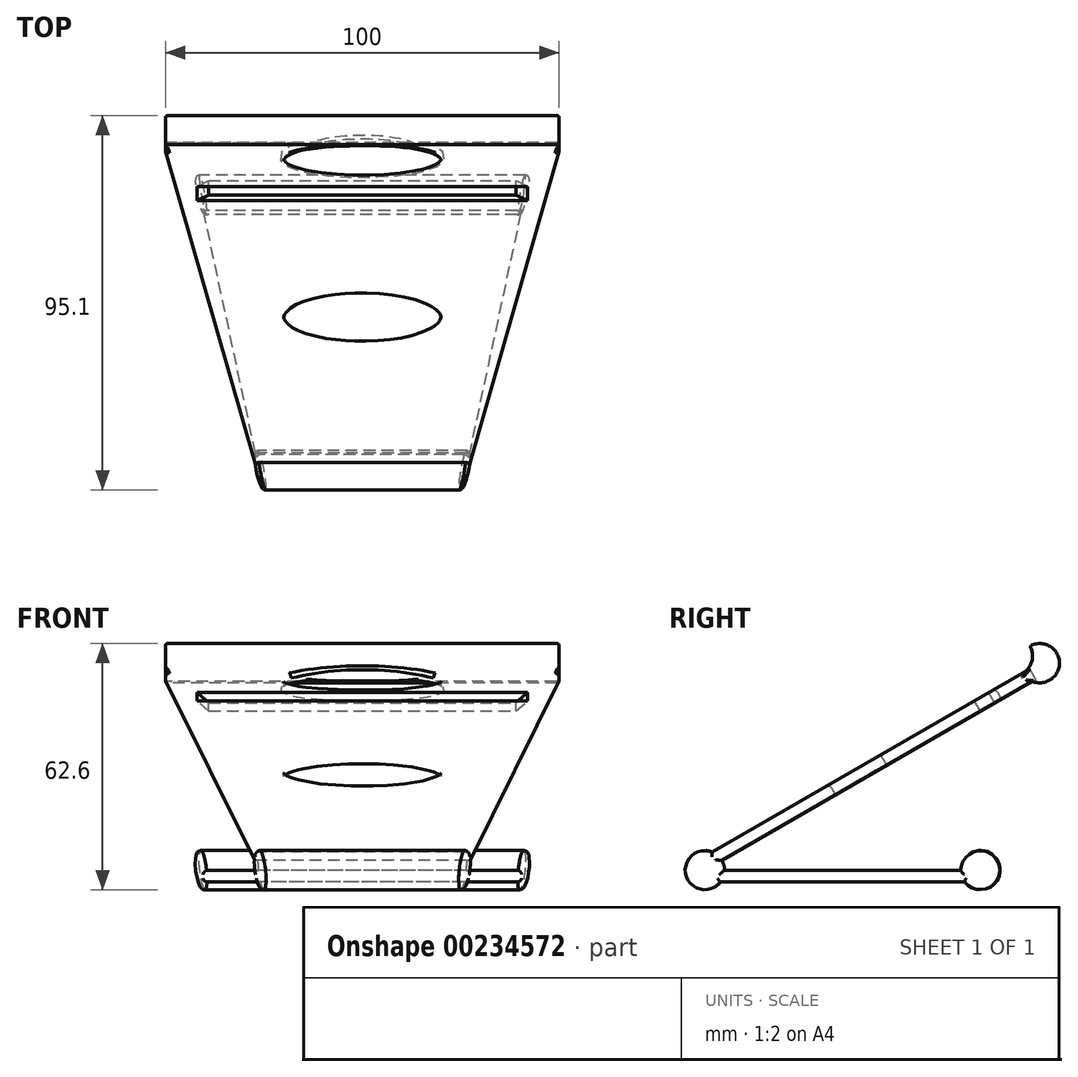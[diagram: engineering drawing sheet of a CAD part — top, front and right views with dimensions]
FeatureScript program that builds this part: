
annotation { "Feature Type Name" : "Feature", "Feature Type Description" : "" }
export const myFeature = defineFeature(function(context is Context, id is Id, definition is map)
    precondition{}
    {
        {
            var Q0;
            Q0=qCreatedBy(makeId("Right.planeOp"),FACE);
            var sketch = newSketch(context, id + "F0", { "sketchPlane" : qUnion([Q0])});
            skLineSegment(sketch, "E0.bottom", {"start": v(-35, -1.5) * mm, "end": v(35, -1.5) * mm});
            skLineSegment(sketch, "E0.top", {"start": v(-35, 1.5) * mm, "end": v(35, 1.5) * mm});
            skLineSegment(sketch, "E0.left", {"start": v(-35, -1.5) * mm, "end": v(-35, 1.5) * mm});
            skLineSegment(sketch, "E0.right", {"start": v(35, -1.5) * mm, "end": v(35, 1.5) * mm});
            skPoint(sketch, "E0.middle", {"position": v(0, 0) * mm});
            skLineSegment(sketch, "E1", {"start": v(-35, 1.5) * mm, "end": v(51.6, 51.5) * mm});
            skLineSegment(sketch, "E2", {"start": v(51.6, 51.5) * mm, "end": v(50.1, 54.1) * mm});
            skLineSegment(sketch, "E3", {"start": v(50.1, 54.1) * mm, "end": v(-36.5, 4.1) * mm});
            skLineSegment(sketch, "E4", {"start": v(-36.5, 4.1) * mm, "end": v(-35, 1.5) * mm});
            skCircle(sketch, "E5", {"center": v(-35, 1.5) * mm, "radius": 5 * mm});
            skCircle(sketch, "E6", {"center": v(35, 1.5) * mm, "radius": 5 * mm});
            skCircle(sketch, "E7", {"center": v(50.1, 54.1) * mm, "radius": 5 * mm});
            skLineSegment(sketch, "E8", {"start": v(47.6, 58.43) * mm, "end": v(47.6, 58.43) * mm});
            skLineSegment(sketch, "E9", {"start": v(45.77, 51.6) * mm, "end": v(45.77, 51.6) * mm});
            skArc(sketch, "E10.filletArc", {"start": v(45.77, 51.6) * mm, "mid": v(48.1, 54.63) * mm, "end": v(47.6, 58.43) * mm});
            skSolve(sketch);
        }
        {
            var Q0;
            {var subQ0=sQuery(id+"F0.wireOp",EDGE,"E0.right");Q0=makeQuery(id+"F0.imprint","IMPRINT",FACE,{"disambiguationData":[TD([[makeQuery(id+"F0.imprint","IMPRINT",EDGE,{"derivedFrom":subQ0}),-1.0]])]});}
            var Q1;
            {var subQ6=sQuery(id+"F0.wireOp",EDGE,"E0.left");Q1=makeQuery(id+"F0.imprint","IMPRINT",FACE,{"disambiguationData":[TD([[makeQuery(id+"F0.imprint","IMPRINT",EDGE,{"derivedFrom":subQ6}),1.0]])]});}
            var Q2;
            {var subQ0=sQuery(id+"F0.wireOp",EDGE,"E5");var subQ1=sQuery(id+"F0.wireOp",EDGE,"E0.bottom");var subQ2=makeQuery(id+"F0.imprint","INTERSECT",VERTEX,{"derivedFrom":[subQ1,subQ0]});Q2=makeQuery(id+"F0.imprint","IMPRINT",FACE,{"disambiguationData":[TD([[makeQuery(id+"F0.imprint","IMPRINT",EDGE,{"disambiguationData":[TD([[subQ2,-1.0]])],"derivedFrom":subQ1}),1.0]])]});}
            var Q3;
            {var subQ0=sQuery(id+"F0.wireOp",EDGE,"E0.right");Q3=makeQuery(id+"F0.imprint","IMPRINT",FACE,{"disambiguationData":[TD([[makeQuery(id+"F0.imprint","IMPRINT",EDGE,{"derivedFrom":subQ0}),1.0]])]});}
            var Q4;
            {var subQ1=sQuery(id+"F0.wireOp",EDGE,"E0.top");var subQ3=sQuery(id+"F0.wireOp",EDGE,"E5");var subQ4=makeQuery(id+"F0.imprint","INTERSECT",VERTEX,{"derivedFrom":[subQ1,subQ3]});Q4=makeQuery(id+"F0.imprint","IMPRINT",FACE,{"disambiguationData":[TD([[makeQuery(id+"F0.imprint","IMPRINT",EDGE,{"disambiguationData":[TD([[subQ4,-1.0]])],"derivedFrom":subQ3}),1.0]])]});}
            var Q5;
            {var subQ0=sQuery(id+"F0.wireOp",EDGE,"E5");var subQ1=sQuery(id+"F0.wireOp",EDGE,"E1");var subQ2=makeQuery(id+"F0.imprint","INTERSECT",VERTEX,{"derivedFrom":[subQ1,subQ0]});Q5=makeQuery(id+"F0.imprint","IMPRINT",FACE,{"disambiguationData":[TD([[makeQuery(id+"F0.imprint","IMPRINT",EDGE,{"disambiguationData":[TD([[subQ2,-1.0]])],"derivedFrom":subQ1}),1.0]])]});}
            var Q6;
            {var subQ0=sQuery(id+"F0.wireOp",EDGE,"E2");Q6=makeQuery(id+"F0.imprint","IMPRINT",FACE,{"disambiguationData":[TD([[makeQuery(id+"F0.imprint","IMPRINT",EDGE,{"derivedFrom":subQ0}),1.0]])]});}
            var Q7;
            {var subQ1=sQuery(id+"F0.wireOp",EDGE,"E2");Q7=makeQuery(id+"F0.imprint","IMPRINT",FACE,{"disambiguationData":[TD([[makeQuery(id+"F0.imprint","IMPRINT",EDGE,{"derivedFrom":subQ1}),-1.0]])]});}
            var Q8;
            {var subQ0=sQuery(id+"F0.wireOp",EDGE,"E0.left");Q8=makeQuery(id+"F0.imprint","IMPRINT",FACE,{"disambiguationData":[TD([[makeQuery(id+"F0.imprint","IMPRINT",EDGE,{"derivedFrom":subQ0}),-1.0]])]});}
            var Q9;
            {var subQ0=sQuery(id+"F0.wireOp",EDGE,"E4");Q9=makeQuery(id+"F0.imprint","IMPRINT",FACE,{"disambiguationData":[TD([[makeQuery(id+"F0.imprint","IMPRINT",EDGE,{"derivedFrom":subQ0}),1.0]])]});}
            extrude(context, id + "F1", {"entities" : qUnion([Q0, Q1, Q2, Q3, Q4, Q5, Q6, Q7, Q8, Q9]), "depth" : 100 * mm});
        }
        {
            var Q0;
            Q0=makeQuery(id+"F1.opExtrude","SWEPT_FACE",FACE,{"disambiguationData":[OSD([sQuery(id+"F0.wireOp",EDGE,"E3")])]});
            var sketch = newSketch(context, id + "F2", { "sketchPlane" : qUnion([Q0])});
            skLineSegment(sketch, "E11", {"start": v(50, -25.56) * mm, "end": v(50, 65.44) * mm, "construction": true});
            skLineSegment(sketch, "E12.bottom", {"start": v(11, 51.24) * mm, "end": v(89, 51.24) * mm});
            skLineSegment(sketch, "E12.top", {"start": v(11, 55.44) * mm, "end": v(89, 55.44) * mm});
            skLineSegment(sketch, "E12.left", {"start": v(11, 51.24) * mm, "end": v(11, 55.44) * mm});
            skLineSegment(sketch, "E12.right", {"start": v(89, 51.24) * mm, "end": v(89, 55.44) * mm});
            skPoint(sketch, "E12.middle", {"position": v(50, 53.34) * mm});
            skLineSegment(sketch, "E13.bottom", {"start": v(0, 65.44) * mm, "end": v(100, 65.44) * mm});
            skLineSegment(sketch, "E13.top", {"start": v(0, -35.56) * mm, "end": v(100, -35.56) * mm});
            skLineSegment(sketch, "E13.left", {"start": v(0, 65.44) * mm, "end": v(0, -35.56) * mm});
            skLineSegment(sketch, "E13.right", {"start": v(100, 65.44) * mm, "end": v(100, -35.56) * mm});
            skLineSegment(sketch, "E14", {"start": v(0, 65.44) * mm, "end": v(25, -35.56) * mm});
            skLineSegment(sketch, "E15", {"start": v(25, -35.56) * mm, "end": v(75, -35.56) * mm});
            skLineSegment(sketch, "E16", {"start": v(75, -35.56) * mm, "end": v(100, 65.44) * mm});
            skEllipse(sketch, "E17", {"center": v(50, 62.44) * mm, "majorRadius": 20 * mm, "minorRadius": 5 * mm, "majorAxis": v(-1, 0)});
            skEllipse(sketch, "E18", {"center": v(50, 16.24) * mm, "majorRadius": 20 * mm, "minorRadius": 7.5 * mm, "majorAxis": v(-1, 0)});
            skSolve(sketch);
        }
        {
            var Q0;
            Q0=makeQuery(id+"F2.imprint","IMPRINT",FACE,{"disambiguationData":[TD([[makeQuery(id+"F2.imprint","IMPRINT",EDGE,{"derivedFrom":sQuery(id+"F2.wireOp",EDGE,"E18")}),1.0]])]});
            var Q1;
            Q1=makeQuery(id+"F2.imprint","IMPRINT",FACE,{"disambiguationData":[TD([[makeQuery(id+"F2.imprint","IMPRINT",EDGE,{"derivedFrom":sQuery(id+"F2.wireOp",EDGE,"E12.bottom")}),1.0]])]});
            var Q2;
            Q2=makeQuery(id+"F2.imprint","IMPRINT",FACE,{"disambiguationData":[TD([[makeQuery(id+"F2.imprint","IMPRINT",EDGE,{"derivedFrom":sQuery(id+"F2.wireOp",EDGE,"E17")}),1.0]])]});
            extrude(context, id + "F3", {"entities" : qUnion([Q0, Q1, Q2]), "operationType" : NewBodyOperationType.REMOVE, "endBound" : BoundingType.SYMMETRIC, "oppositeDirection" : true, "depth" : 20 * mm});
        }
        {
            var Q0;
            {var subQ0=sQuery(id+"F2.wireOp",EDGE,"E14");var subQ1=sQuery(id+"F2.wireOp",EDGE,"E13.left");var subQ2=makeQuery(id+"F2.imprint","INTERSECT",VERTEX,{"derivedFrom":[sQuery(id+"F2.wireOp",EDGE,"E13.bottom"),subQ1,subQ0]});Q0=makeQuery(id+"F2.imprint","IMPRINT",FACE,{"disambiguationData":[TD([[makeQuery(id+"F2.imprint","IMPRINT",EDGE,{"disambiguationData":[TD([[subQ2,-1.0]])],"derivedFrom":subQ1}),1.0]])]});}
            var Q1;
            {var subQ0=sQuery(id+"F2.wireOp",EDGE,"E13.left");var subQ1=sQuery(id+"F2.wireOp",EDGE,"E13.top");var subQ2=makeQuery(id+"F2.imprint","INTERSECT",VERTEX,{"derivedFrom":[subQ1,subQ0]});Q1=makeQuery(id+"F2.imprint","IMPRINT",FACE,{"disambiguationData":[TD([[makeQuery(id+"F2.imprint","IMPRINT",EDGE,{"disambiguationData":[TD([[subQ2,-1.0]])],"derivedFrom":subQ1}),1.0]])]});}
            var Q2;
            {var subQ0=sQuery(id+"F2.wireOp",EDGE,"E13.right");var subQ1=sQuery(id+"F2.wireOp",EDGE,"E13.top");var subQ2=makeQuery(id+"F2.imprint","INTERSECT",VERTEX,{"derivedFrom":[subQ1,subQ0]});Q2=makeQuery(id+"F2.imprint","IMPRINT",FACE,{"disambiguationData":[TD([[makeQuery(id+"F2.imprint","IMPRINT",EDGE,{"disambiguationData":[TD([[subQ2,1.0]])],"derivedFrom":subQ1}),1.0]])]});}
            var Q3;
            {var subQ0=sQuery(id+"F2.wireOp",EDGE,"E16");var subQ1=sQuery(id+"F2.wireOp",EDGE,"E13.right");var subQ2=makeQuery(id+"F2.imprint","INTERSECT",VERTEX,{"derivedFrom":[sQuery(id+"F2.wireOp",EDGE,"E13.bottom"),subQ1,subQ0]});Q3=makeQuery(id+"F2.imprint","IMPRINT",FACE,{"disambiguationData":[TD([[makeQuery(id+"F2.imprint","IMPRINT",EDGE,{"disambiguationData":[TD([[subQ2,-1.0]])],"derivedFrom":subQ1}),-1.0]])]});}
            extrude(context, id + "F4", {"entities" : qUnion([Q0, Q1, Q2, Q3]), "operationType" : NewBodyOperationType.REMOVE, "endBound" : BoundingType.SYMMETRIC, "oppositeDirection" : true, "depth" : 100 * mm});
        }
        {
            var Q0;
            Q0=makeQuery(id+"F4.boolean.opBoolean","COPY",FACE,{"derivedFrom":makeQuery(id+"F4.opExtrude","SWEPT_FACE",FACE,{"disambiguationData":[OSD([sQuery(id+"F2.wireOp",EDGE,"E16")])]})});
            var Q1;
            Q1=makeQuery(id+"F4.boolean.opBoolean","COPY",FACE,{"derivedFrom":makeQuery(id+"F4.opExtrude","SWEPT_FACE",FACE,{"disambiguationData":[OSD([sQuery(id+"F2.wireOp",EDGE,"E14")])]})});
            var Q2;
            Q2=makeQuery(id+"F3.boolean.opBoolean","COPY",FACE,{"derivedFrom":makeQuery(id+"F3.opExtrude","SWEPT_FACE",FACE,{"disambiguationData":[OSD([sQuery(id+"F2.wireOp",EDGE,"E18")])]})});
            var Q3;
            Q3=makeQuery(id+"F3.boolean.opBoolean","COPY",FACE,{"derivedFrom":makeQuery(id+"F3.opExtrude","SWEPT_FACE",FACE,{"disambiguationData":[OSD([sQuery(id+"F2.wireOp",EDGE,"E17")])]})});
            fillet(context, id + "F5", {"entities" : qUnion([Q0, Q1, Q2, Q3]), "radius" : 1 * mm, "tangentPropagation" : true, "allowEdgeOverflow" : false});
        }
        {
            var Q0;
            Q0=makeQuery(id+"F1.opExtrude","CAP_FACE",FACE,{"disambiguationData":[OSD([sQuery(id+"F0.wireOp",EDGE,"E0.bottom"),sQuery(id+"F0.wireOp",EDGE,"E0.top"),sQuery(id+"F0.wireOp",EDGE,"E1"),sQuery(id+"F0.wireOp",EDGE,"E3"),sQuery(id+"F0.wireOp",EDGE,"E5"),sQuery(id+"F0.wireOp",EDGE,"E6"),sQuery(id+"F0.wireOp",EDGE,"E7"),sQuery(id+"F0.wireOp",EDGE,"E10.filletArc")])],"isStart":true});
            var Q1;
            Q1=makeQuery(id+"F1.opExtrude","CAP_FACE",FACE,{"disambiguationData":[OSD([sQuery(id+"F0.wireOp",EDGE,"E0.bottom"),sQuery(id+"F0.wireOp",EDGE,"E0.top"),sQuery(id+"F0.wireOp",EDGE,"E1"),sQuery(id+"F0.wireOp",EDGE,"E3"),sQuery(id+"F0.wireOp",EDGE,"E5"),sQuery(id+"F0.wireOp",EDGE,"E6"),sQuery(id+"F0.wireOp",EDGE,"E7"),sQuery(id+"F0.wireOp",EDGE,"E10.filletArc")])],"isStart":false});
            var Q2;
            Q2=makeQuery(id+"F1.opExtrude","SWEPT_EDGE",EDGE,{"disambiguationData":[OSD([sQuery(id+"F0.wireOp",EDGE,"E7"),sQuery(id+"F0.wireOp",EDGE,"E10.filletArc")])]});
            fillet(context, id + "F6", {"entities" : qUnion([Q0, Q1, Q2]), "radius" : 0.5 * mm, "tangentPropagation" : true, "allowEdgeOverflow" : false});
        }
        {
            var Q0;
            Q0=makeQuery(id+"F3.boolean.opBoolean","INTERSECT",EDGE,{"derivedFrom":[makeQuery(id+"F1.opExtrude","SWEPT_FACE",FACE,{"disambiguationData":[OSD([sQuery(id+"F0.wireOp",EDGE,"E3")])]}),makeQuery(id+"F3.opExtrude","SWEPT_FACE",FACE,{"disambiguationData":[OSD([sQuery(id+"F2.wireOp",EDGE,"E12.left")])]})]});
            var Q1;
            Q1=makeQuery(id+"F3.boolean.opBoolean","INTERSECT",EDGE,{"derivedFrom":[makeQuery(id+"F1.opExtrude","SWEPT_FACE",FACE,{"disambiguationData":[OSD([sQuery(id+"F0.wireOp",EDGE,"E3")])]}),makeQuery(id+"F3.opExtrude","SWEPT_FACE",FACE,{"disambiguationData":[OSD([sQuery(id+"F2.wireOp",EDGE,"E12.right")])]})]});
            chamfer(context, id + "F7", {"entities" : qUnion([Q0, Q1]), "width" : 3 * mm, "tangentPropagation" : true});
        }
    });
